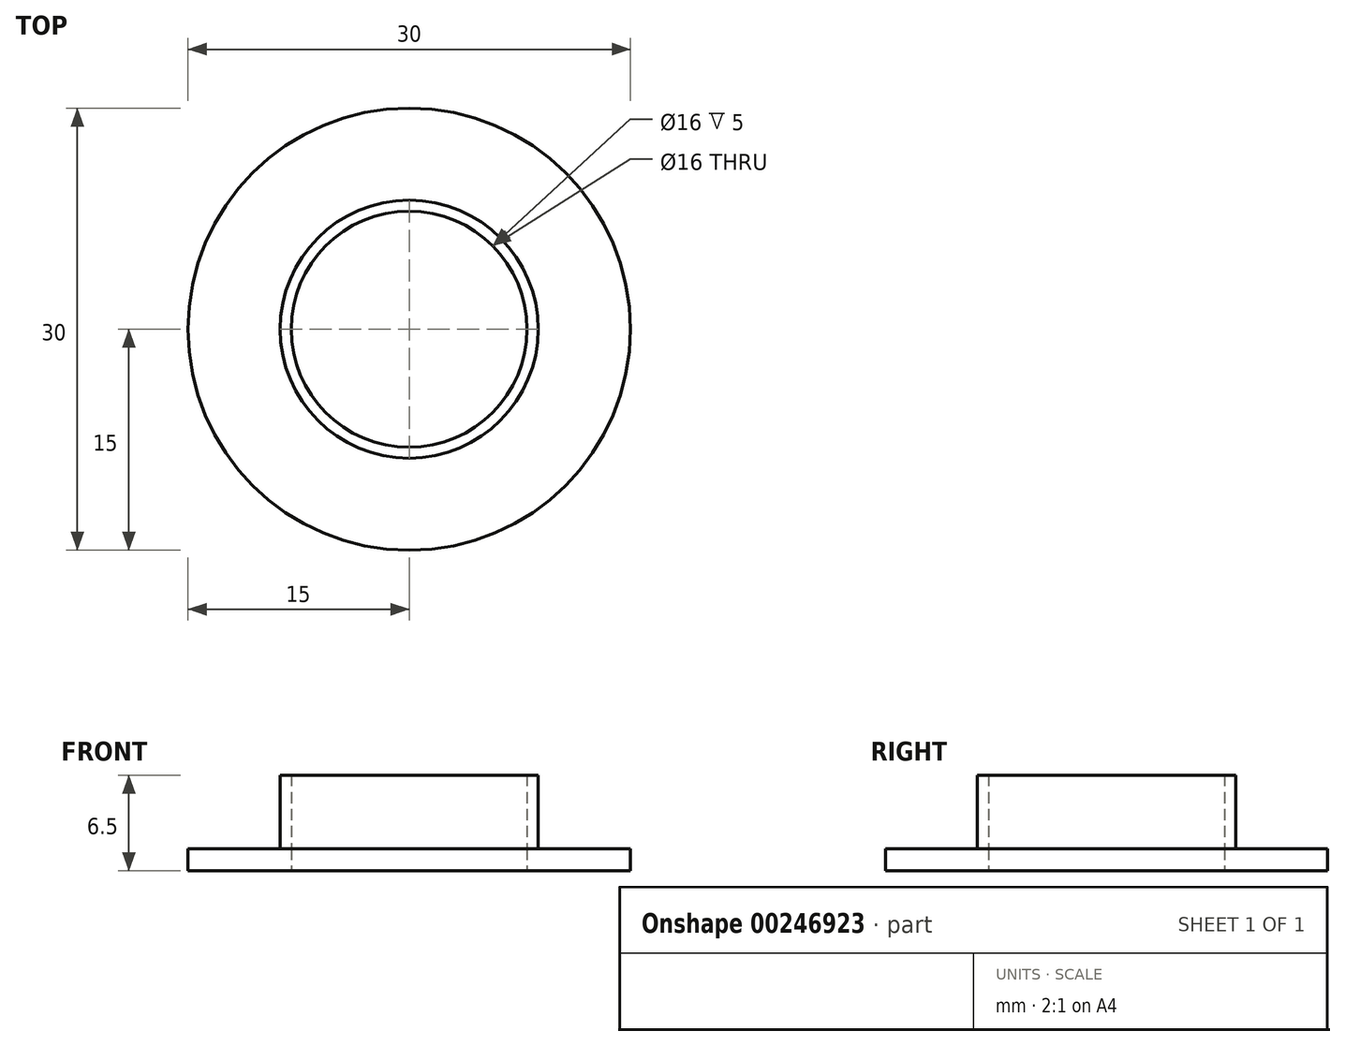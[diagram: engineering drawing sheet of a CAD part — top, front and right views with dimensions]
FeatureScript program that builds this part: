
annotation { "Feature Type Name" : "Feature", "Feature Type Description" : "" }
export const myFeature = defineFeature(function(context is Context, id is Id, definition is map)
    precondition{}
    {
        {
            var Q0;
            Q0=qCreatedBy(makeId("Top.planeOp"),FACE);
            var sketch = newSketch(context, id + "F0", { "sketchPlane" : qUnion([Q0])});
            skCircle(sketch, "E0", {"center": v(0, 0) * mm, "radius": 15 * mm});
            skCircle(sketch, "E1", {"center": v(0, 0) * mm, "radius": 8 * mm});
            skSolve(sketch);
        }
        {
            var Q0;
            Q0 = qSketchRegion(id + "F0", true);
            extrude(context, id + "F1", {"entities" : qUnion([Q0]), "depth" : 1.5 * mm});
        }
        {
            var Q0;
            Q0=makeQuery(id+"F1.opExtrude","CAP_FACE",FACE,{"disambiguationData":[OSD([sQuery(id+"F0.wireOp",EDGE,"E0"),sQuery(id+"F0.wireOp",EDGE,"E1")])],"isStart":false});
            var sketch = newSketch(context, id + "F2", { "sketchPlane" : qUnion([Q0])});
            skCircle(sketch, "E2.0", {"center": v(0, 0) * mm, "radius": 8 * mm});
            skCircle(sketch, "E3", {"center": v(0, 0) * mm, "radius": 8.75 * mm});
            skSolve(sketch);
        }
        {
            var Q0;
            Q0 = qSketchRegion(id + "F2", true);
            extrude(context, id + "F3", {"entities" : qUnion([Q0]), "depth" : 5 * mm});
        }
    });
